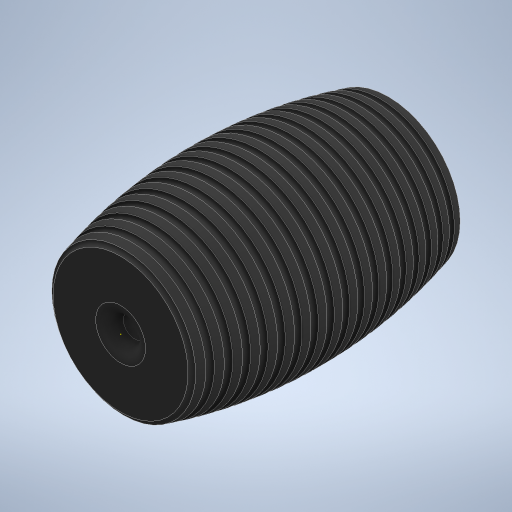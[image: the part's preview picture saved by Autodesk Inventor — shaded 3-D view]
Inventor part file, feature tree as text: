
AUTODESK INVENTOR PART (.ipt)
format: ipt  version: 2024.2 (Build 282272000, 272)  size: 586,240 bytes
history: native  units: mm
features: sketch x2, fillet x2, revolve x1
ambient origin geometry x8: Origin, YZ Plane, XZ Plane, XY Plane, X Axis, Y Axis, Z Axis, Center Point
bodies: Solid1 (feature_tree)
feature tree (5):
  revolve  "Revolution1"  [1 undecoded]
  sketch  "Sketch4"  dims[d4=360.0deg d5=0.5mm d6=2000.0mm d8=360.0deg d17=1.0mm d18=1.0mm d19=0.0mm d20=0.0mm d21=0.0mm]
  fillet  "Fillet1"  Radius=0.8mm
  fillet  "Fillet2"  Radius=35.0mm
  sketch  "Sketch1"  dims[d0=6.5mm d1=19.5mm d2=0.8mm d3=35.0mm]
note: 1 required parameter value undecoded (feature->parameter linkage not recoverable at this tier; creation-order binding heuristic only, values carry confidence <= 0.55)
